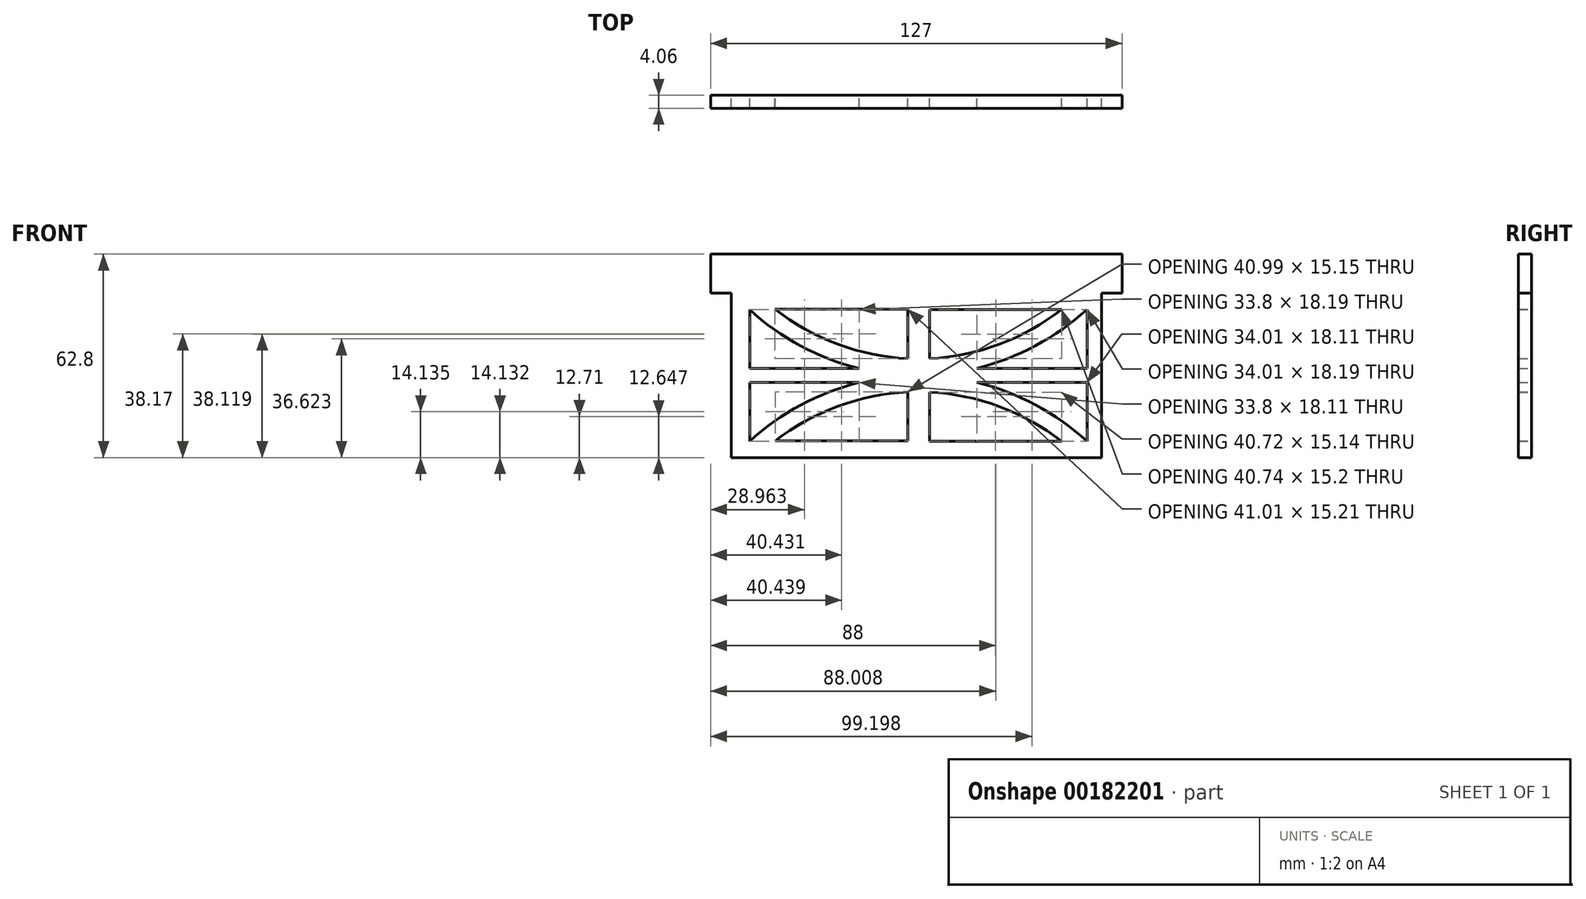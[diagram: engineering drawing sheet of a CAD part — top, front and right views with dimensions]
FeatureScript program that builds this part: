
annotation { "Feature Type Name" : "Feature", "Feature Type Description" : "" }
export const myFeature = defineFeature(function(context is Context, id is Id, definition is map)
    precondition{}
    {
        {
            var Q0;
            Q0=qCreatedBy(makeId("Front.planeOp"),FACE);
            var sketch = newSketch(context, id + "F0", { "sketchPlane" : qUnion([Q0])});
            skLineSegment(sketch, "E0.top", {"start": v(-52.67, -25.95) * mm, "end": v(61.63, -25.95) * mm});
            skLineSegment(sketch, "E0.left", {"start": v(-52.67, 24.85) * mm, "end": v(-52.67, -25.95) * mm});
            skLineSegment(sketch, "E0.right", {"start": v(61.63, 24.85) * mm, "end": v(61.63, -25.95) * mm});
            skLineSegment(sketch, "E1.top", {"start": v(67.98, 36.85) * mm, "end": v(-59.02, 36.85) * mm});
            skLineSegment(sketch, "E1.left", {"start": v(67.98, 24.85) * mm, "end": v(67.98, 36.85) * mm});
            skLineSegment(sketch, "E1.right", {"start": v(-59.02, 24.85) * mm, "end": v(-59.02, 36.85) * mm});
            skLineSegment(sketch, "E2", {"start": v(61.63, 24.85) * mm, "end": v(67.98, 24.85) * mm});
            skLineSegment(sketch, "E3", {"start": v(-52.67, 24.85) * mm, "end": v(-59.02, 24.85) * mm});
            skLineSegment(sketch, "E4", {"start": v(1.92, 4.61) * mm, "end": v(1.92, 19.82) * mm});
            skLineSegment(sketch, "E5", {"start": v(8.62, 19.77) * mm, "end": v(8.62, 4.57) * mm});
            skLineSegment(sketch, "E6", {"start": v(-39.1, 19.82) * mm, "end": v(1.92, 19.82) * mm});
            skLineSegment(sketch, "E7", {"start": v(8.62, 19.77) * mm, "end": v(49.36, 19.77) * mm});
            skLineSegment(sketch, "E8", {"start": v(1.92, -5.66) * mm, "end": v(1.92, -20.82) * mm});
            skLineSegment(sketch, "E9", {"start": v(8.62, -5.73) * mm, "end": v(8.62, -20.87) * mm});
            skLineSegment(sketch, "E10", {"start": v(-39.08, -20.82) * mm, "end": v(1.92, -20.82) * mm});
            skLineSegment(sketch, "E11", {"start": v(8.62, -20.87) * mm, "end": v(49.34, -20.87) * mm});
            skArc(sketch, "E12", {"start": v(-39.1, 19.82) * mm, "mid": v(-19.76, 9.06) * mm, "end": v(1.92, 4.61) * mm});
            skArc(sketch, "E13", {"start": v(8.62, 4.57) * mm, "mid": v(30.15, 9.04) * mm, "end": v(49.36, 19.77) * mm});
            skArc(sketch, "E14", {"start": v(1.92, -5.66) * mm, "mid": v(-19.72, -10.15) * mm, "end": v(-39.08, -20.82) * mm});
            skArc(sketch, "E15", {"start": v(49.34, -20.87) * mm, "mid": v(30.14, -10.2) * mm, "end": v(8.62, -5.73) * mm});
            skLineSegment(sketch, "E16", {"start": v(-13.16, 1.58) * mm, "end": v(-46.96, 1.58) * mm});
            skLineSegment(sketch, "E17", {"start": v(-13.16, -2.76) * mm, "end": v(-46.96, -2.76) * mm});
            skLineSegment(sketch, "E18", {"start": v(23.17, 1.58) * mm, "end": v(57.18, 1.58) * mm});
            skLineSegment(sketch, "E19", {"start": v(23.17, -2.76) * mm, "end": v(57.18, -2.76) * mm});
            skLineSegment(sketch, "E20", {"start": v(57.18, 19.77) * mm, "end": v(57.18, 1.58) * mm});
            skLineSegment(sketch, "E21", {"start": v(-46.96, 19.77) * mm, "end": v(-46.96, 1.58) * mm});
            skLineSegment(sketch, "E22", {"start": v(-46.96, -2.76) * mm, "end": v(-46.96, -20.87) * mm});
            skArc(sketch, "E23", {"start": v(-46.96, 19.77) * mm, "mid": v(-31.22, 8.52) * mm, "end": v(-13.16, 1.58) * mm});
            skArc(sketch, "E24", {"start": v(-13.16, -2.76) * mm, "mid": v(-31.16, -9.75) * mm, "end": v(-46.96, -20.87) * mm});
            skArc(sketch, "E25", {"start": v(23.17, 1.58) * mm, "mid": v(41.3, 8.59) * mm, "end": v(57.18, 19.77) * mm});
            skArc(sketch, "E26", {"start": v(57.18, -20.87) * mm, "mid": v(41.32, -9.68) * mm, "end": v(23.17, -2.76) * mm});
            skLineSegment(sketch, "E27", {"start": v(57.18, -20.87) * mm, "end": v(57.18, -2.76) * mm});
            skSolve(sketch);
        }
        {
            var Q0;
            Q0=makeQuery(id+"F0.imprint","IMPRINT",FACE,{"disambiguationData":[TD([[makeQuery(id+"F0.imprint","IMPRINT",EDGE,{"derivedFrom":sQuery(id+"F0.wireOp",EDGE,"E0.top")}),1.0]])]});
            extrude(context, id + "F1", {"entities" : qUnion([Q0]), "depth" : 4.06 * mm});
        }
    });
